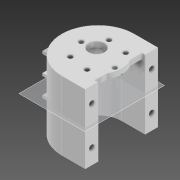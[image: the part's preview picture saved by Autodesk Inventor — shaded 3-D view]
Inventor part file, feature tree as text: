
AUTODESK INVENTOR PART (.ipt)
format: ipt  version: 2020 (Build 240168000, 168)  size: 246,784 bytes
history: native  units: in
note: dims shown in document units (in); Inventor stores cm internally (conversion verified against a paired STEP export)
features: sketch x5, extrude x4, pattern_linear x2, plane x1, mirror x1
ambient origin geometry x8: Origin, YZ Plane, XZ Plane, XY Plane, X Axis, Y Axis, Z Axis, Center Point
bodies: Solid1 (feature_tree)
feature tree (13):
  sketch  "Sketch1"  dims[d2=0.4882in d4=0.2362in]
  extrude  "Extrusion1"  Depth=0.2362in
  extrude  "Extrusion2"  Depth=0.2756in
  sketch  "Sketch2"  dims[d5=3.1496in d13=0.2756in]
  plane  "Work Plane1"
  extrude  "Extrusion3"  Depth=1.4567in
  pattern_linear  "Rectangular Pattern1"  Spacing1=0.3937in  [1 undecoded]
  pattern_linear  "Rectangular Pattern2"  Spacing1=0.1575in  [1 undecoded]
  extrude  "Extrusion4"  Depth=1.9685in TaperAngle=0.0deg
  mirror  "Mirror1"
  sketch  "Sketch7"  dims[d19=0.3937in d20=0.3937in d22=0.1575in d23=0.0in d24=1.9685in d25=0.0in d26=-1.0236in d31=0.3937in d32=0.7874in d33=0.1969in d34=0.1969in d35=0.1181in d36=0.0394in d37=0.1181in d38=0.1181in d39=0.0394in d40=0.1181in d41=0.0394in d42=0.0787in d43=0.0in d44=0.7874in d46=0.5906in d47=0.7874in d49=0.5906in d50=0.1969in d51=0.5906in d52=1.1811in d53=0.1575in d54=0.1575in d55=0.5906in d56=0.0in d58=0.2617in d59=1.2205in d63=1.905in d65=0.7926in d66=0.1378in d67=2.3622in d69=360.0deg]
  sketch  "Sketch5"  dims[d14=0.9606in d17=1.4567in]
  sketch  "Sketch6"  dims[d18=1.122in]
note: 2 required parameter values undecoded (feature->parameter linkage not recoverable at this tier; creation-order binding heuristic only, values carry confidence <= 0.55)
